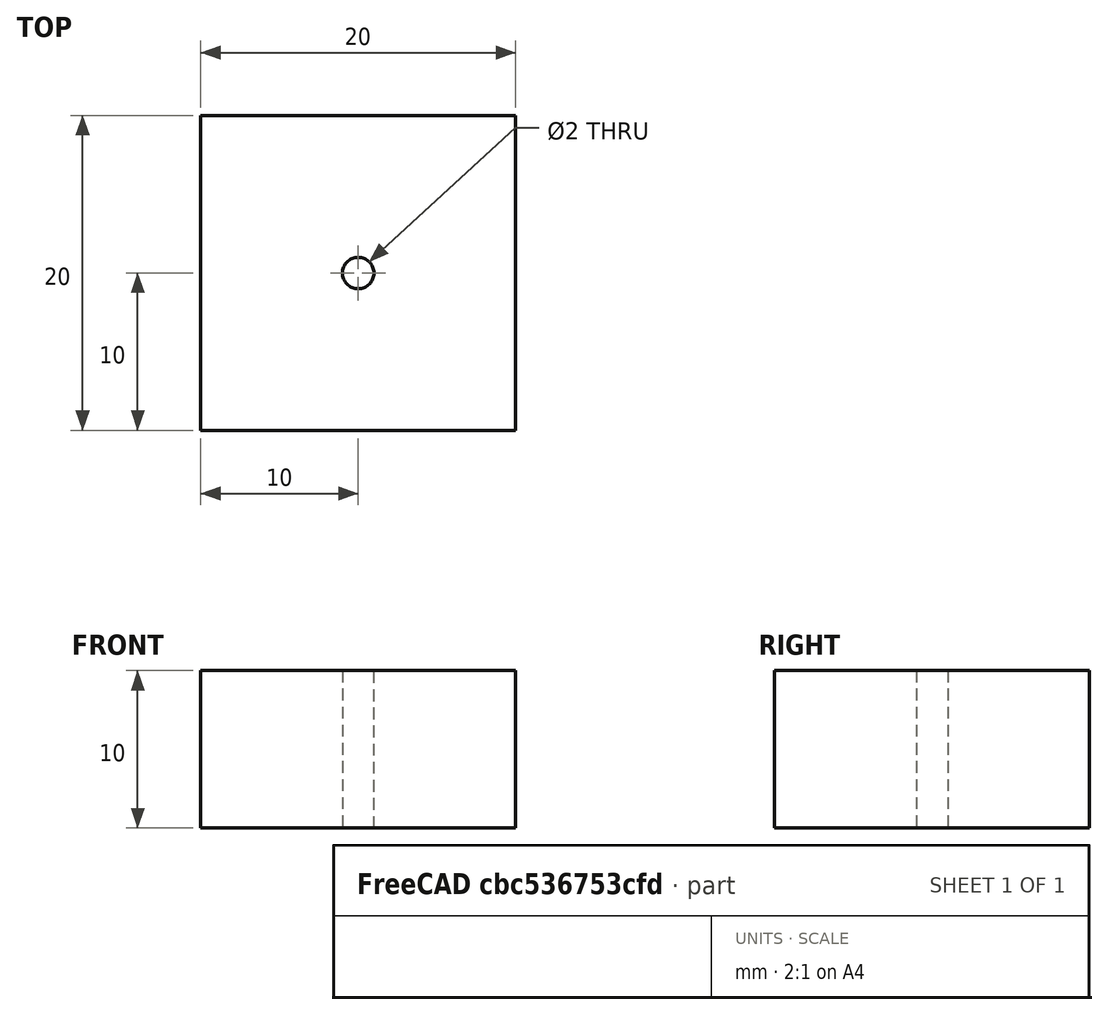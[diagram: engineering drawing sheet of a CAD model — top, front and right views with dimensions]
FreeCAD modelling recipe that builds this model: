
FCSTD DOCUMENT  (FreeCAD 1.0R38806 (Git))
Label: taladrado
License: All rights reserved
LicenseURL: https://en.wikipedia.org/wiki/All_rights_reserved
objects: Sketcher::SketchObject×1, Part::Extrusion×1
note: 3 computed .brp shape members not serialized (recipe doc carries the construction recipe); baked Part::Feature solids carry a one-line shape summary decoded from their .brp

FEATURE [Sketcher::SketchObject] Sketch
  ArcFitTolerance = 1e-06
  FullyConstrained = true
  MakeInternals = false
  sketch-geometry (6):
    g0: LineSegment StartX=-10 StartY=-10 StartZ=0 EndX=10 EndY=-10 EndZ=0
    g1: LineSegment StartX=10 StartY=-10 StartZ=0 EndX=10 EndY=10 EndZ=0
    g2: LineSegment StartX=10 StartY=10 StartZ=0 EndX=-10 EndY=10 EndZ=0
    g3: LineSegment StartX=-10 StartY=10 StartZ=0 EndX=-10 EndY=-10 EndZ=0
    g4: GeomPoint [constr] X=-1.4e-15 Y=0 Z=0
    g5: Circle CenterX=-1.4e-15 CenterY=0 CenterZ=0 NormalX=0 NormalY=0 NormalZ=1 AngleXU=0 Radius=1
  constraints (14):
    c: Coincident(g0,g1)
    c: Coincident(g1,g2)
    c: Coincident(g2,g3)
    c: Coincident(g3,g0)
    c: Horizontal(g0)
    c: Horizontal(g2)
    c: Vertical(g1)
    c: Vertical(g3)
    c: Symmetric(g2,g0,g4)
    c: Coincident(g4,g-1)
    c: Equal(g2,g1)
    c: Distance(g2,g2) = 20
    c: Coincident(g5,g4)
    c: Diameter(g5) = 2
FEATURE [Part::Extrusion] Extrude
  Base = -> Sketch
  Dir = (0,0,1)
  DirMode = 2
  FaceMakerClass = Part::FaceMakerBullseye
  FaceMakerMode = 3
  LengthFwd = 10
  LengthRev = 0
  Solid = true
  Symmetric = false
